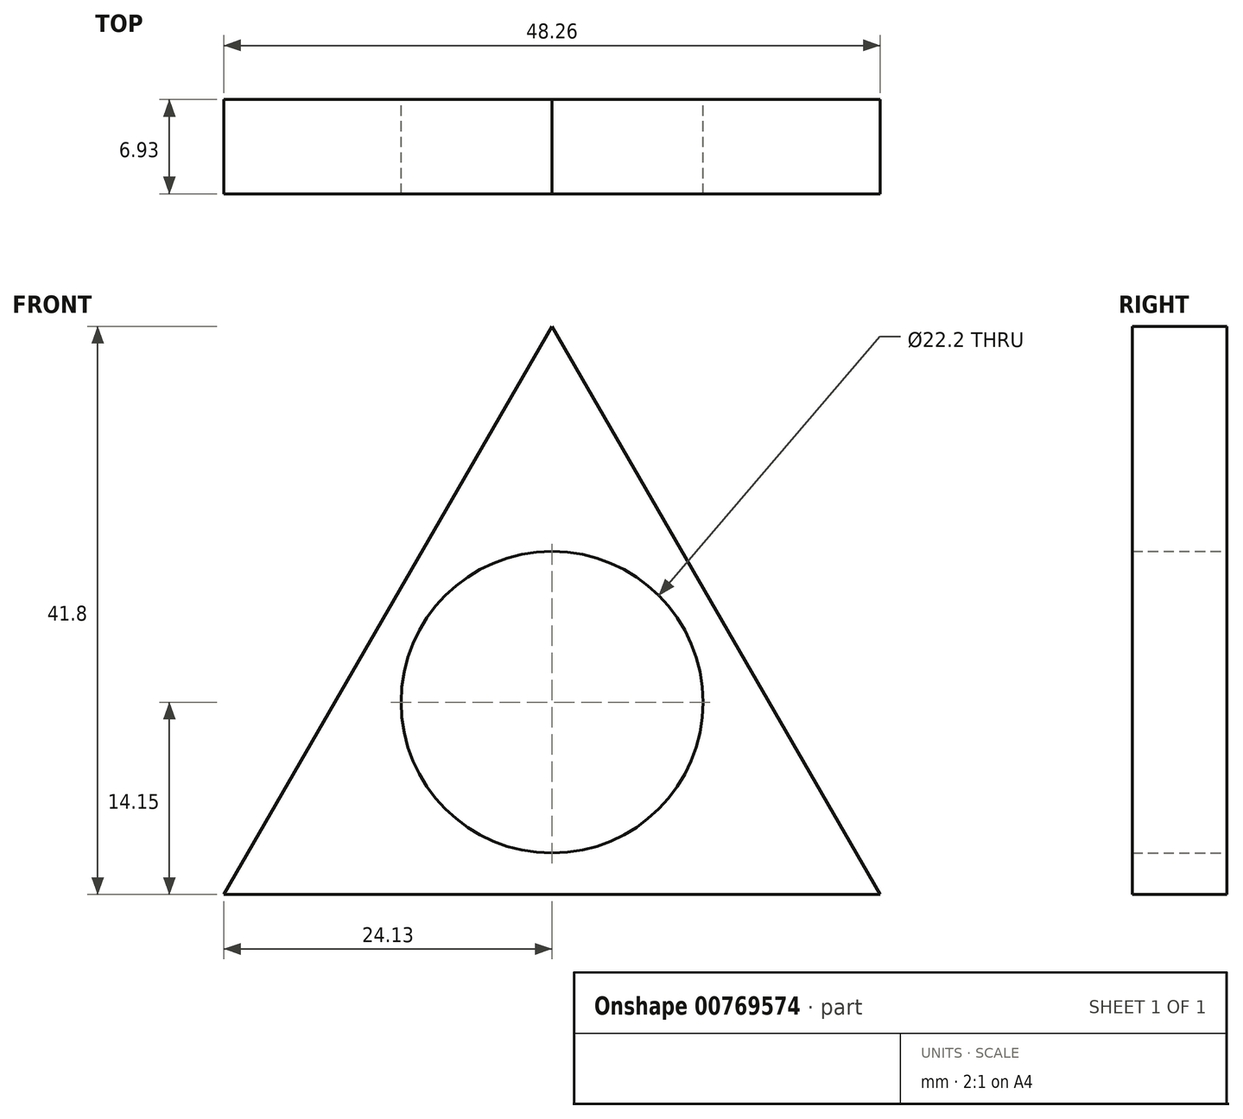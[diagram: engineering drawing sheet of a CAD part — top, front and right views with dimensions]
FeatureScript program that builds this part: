
annotation { "Feature Type Name" : "Feature", "Feature Type Description" : "" }
export const myFeature = defineFeature(function(context is Context, id is Id, definition is map)
    precondition{}
    {
        {
            var Q0;
            Q0=qCreatedBy(makeId("Front.planeOp"),FACE);
            var sketch = newSketch(context, id + "F0", { "sketchPlane" : qUnion([Q0])});
            skLineSegment(sketch, "E0", {"start": v(0, 27.65) * mm, "end": v(-24.13, -14.15) * mm});
            skLineSegment(sketch, "E1", {"start": v(-24.13, -14.15) * mm, "end": v(24.13, -14.15) * mm});
            skLineSegment(sketch, "E2", {"start": v(24.13, -14.15) * mm, "end": v(0, 27.65) * mm});
            skCircle(sketch, "E3", {"center": v(0, 0) * mm, "radius": 11.1 * mm});
            skSolve(sketch);
        }
        {
            var Q0;
            Q0=makeQuery(id+"F0.imprint","IMPRINT",FACE,{"disambiguationData":[TD([[makeQuery(id+"F0.imprint","IMPRINT",EDGE,{"derivedFrom":sQuery(id+"F0.wireOp",EDGE,"E0")}),1.0]])]});
            extrude(context, id + "F1", {"entities" : qUnion([Q0]), "depth" : 6.93 * mm, "offsetDistance" : 25.4 * mm});
        }
    });
